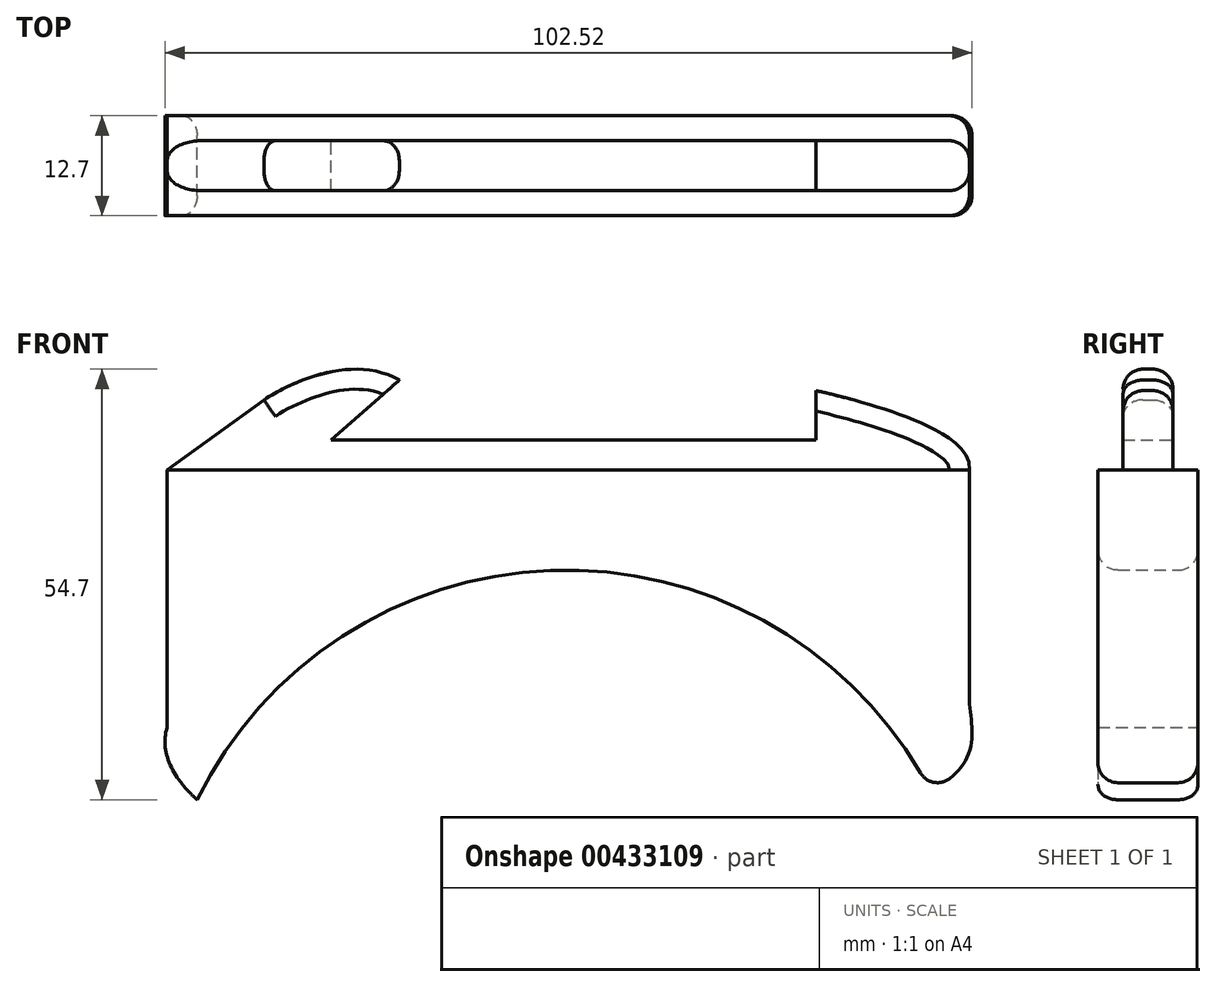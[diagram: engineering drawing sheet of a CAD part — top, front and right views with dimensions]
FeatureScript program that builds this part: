
annotation { "Feature Type Name" : "Feature", "Feature Type Description" : "" }
export const myFeature = defineFeature(function(context is Context, id is Id, definition is map)
    precondition{}
    {
        {
            var Q0;
            Q0=qCreatedBy(makeId("Front.planeOp"),FACE);
            var sketch = newSketch(context, id + "F0", { "sketchPlane" : qUnion([Q0])});
            skLineSegment(sketch, "E0.bottom", {"start": v(-50.95, 22.84) * mm, "end": v(50.95, 22.84) * mm});
            skLineSegment(sketch, "E0.left", {"start": v(-50.95, 22.84) * mm, "end": v(-50.95, -9.85) * mm});
            skLineSegment(sketch, "E0.right", {"start": v(50.95, 22.84) * mm, "end": v(50.95, -5.9) * mm});
            skPoint(sketch, "E0.middle", {"position": v(0, 0) * mm});
            skLineSegment(sketch, "E1", {"start": v(-50.95, 22.84) * mm, "end": v(-38.65, 31.76) * mm});
            skPoint(sketch, "E2.visualSharp", {"position": v(-50.95, -22.84) * mm});
            skPoint(sketch, "E3.visualSharp", {"position": v(50.95, -22.84) * mm});
            skArc(sketch, "E4", {"start": v(46, -17.88) * mm, "mid": v(-0.93, 10.13) * mm, "end": v(-47.15, -19.04) * mm});
            skFitSpline(sketch, "E5", {"points": [v(-50.95, -9.85) * mm, v(-47.15, -19.04) * mm], "startDerivative": vector(-2.84, -9.36) * mm, "endDerivative": vector(9.38, -8.46) * mm});
            skFitSpline(sketch, "E6", {"points": [v(50.95, -5.9) * mm, v(46, -17.88) * mm], "startDerivative": vector(0, -10.68) * mm, "endDerivative": vector(-21.78, -10.66) * mm});
            skLineSegment(sketch, "E7", {"start": v(-21.45, 34.28) * mm, "end": v(-30.14, 26.66) * mm});
            skLineSegment(sketch, "E8", {"start": v(-30.14, 26.66) * mm, "end": v(31.5, 26.66) * mm});
            skLineSegment(sketch, "E9", {"start": v(31.5, 26.66) * mm, "end": v(31.5, 32.95) * mm});
            skFitSpline(sketch, "E10", {"points": [v(-38.65, 31.76) * mm, v(-21.45, 34.28) * mm], "startDerivative": vector(9.73, 6.49) * mm, "endDerivative": vector(17.96, -10.28) * mm});
            skFitSpline(sketch, "E11", {"points": [v(31.5, 32.95) * mm, v(50.95, 22.84) * mm], "startDerivative": vector(38.11, -8.82) * mm, "endDerivative": vector(-1.22, -11.35) * mm});
            skSolve(sketch);
        }
        {
            var Q0;
            Q0=makeQuery(id+"F0.imprint","IMPRINT",FACE,{"disambiguationData":[TD([[makeQuery(id+"F0.imprint","IMPRINT",EDGE,{"derivedFrom":sQuery(id+"F0.wireOp",EDGE,"E0.bottom")}),-1.0]])]});
            extrude(context, id + "F1", {"entities" : qUnion([Q0]), "endBound" : BoundingType.SYMMETRIC, "depth" : 12.7 * mm});
        }
        {
            var Q0;
            Q0=makeQuery(id+"F0.imprint","IMPRINT",FACE,{"disambiguationData":[TD([[makeQuery(id+"F0.imprint","IMPRINT",EDGE,{"derivedFrom":sQuery(id+"F0.wireOp",EDGE,"E0.bottom")}),1.0]])]});
            extrude(context, id + "F2", {"entities" : qUnion([Q0]), "operationType" : NewBodyOperationType.ADD, "endBound" : BoundingType.SYMMETRIC, "depth" : 6.35 * mm});
        }
        {
            var Q0;
            Q0=makeQuery(id+"F1.opExtrude","CAP_EDGE",EDGE,{"disambiguationData":[OSD([sQuery(id+"F0.wireOp",EDGE,"E0.right")])],"isStart":false});
            var Q1;
            Q1=makeQuery(id+"F1.opExtrude","CAP_EDGE",EDGE,{"disambiguationData":[OSD([sQuery(id+"F0.wireOp",EDGE,"E0.right")])],"isStart":true});
            fillet(context, id + "F3", {"entities" : qUnion([Q0, Q1]), "radius" : 2.54 * mm, "tangentPropagation" : true, "allowEdgeOverflow" : false});
        }
        {
            var Q0;
            Q0=makeQuery(id+"F2.opExtrude","CAP_EDGE",EDGE,{"disambiguationData":[OSD([sQuery(id+"F0.wireOp",EDGE,"E11")])],"isStart":false});
            var Q1;
            Q1=makeQuery(id+"F2.opExtrude","CAP_EDGE",EDGE,{"disambiguationData":[OSD([sQuery(id+"F0.wireOp",EDGE,"E11")])],"isStart":true});
            var Q2;
            Q2=makeQuery(id+"F2.opExtrude","CAP_EDGE",EDGE,{"disambiguationData":[OSD([sQuery(id+"F0.wireOp",EDGE,"E10")])],"isStart":false});
            var Q3;
            Q3=makeQuery(id+"F2.opExtrude","CAP_EDGE",EDGE,{"disambiguationData":[OSD([sQuery(id+"F0.wireOp",EDGE,"E1")])],"isStart":false});
            var Q4;
            Q4=makeQuery(id+"F2.opExtrude","CAP_EDGE",EDGE,{"disambiguationData":[OSD([sQuery(id+"F0.wireOp",EDGE,"E10")])],"isStart":true});
            var Q5;
            Q5=makeQuery(id+"F2.opExtrude","CAP_EDGE",EDGE,{"disambiguationData":[OSD([sQuery(id+"F0.wireOp",EDGE,"E1")])],"isStart":true});
            var Q6;
            Q6=makeQuery(id+"F1.opExtrude","CAP_EDGE",EDGE,{"disambiguationData":[OSD([sQuery(id+"F0.wireOp",EDGE,"E4")])],"isStart":true});
            fillet(context, id + "F4", {"entities" : qUnion([Q0, Q1, Q2, Q3, Q4, Q5, Q6]), "radius" : 2.54 * mm, "tangentPropagation" : true, "allowEdgeOverflow" : false});
        }
    });
